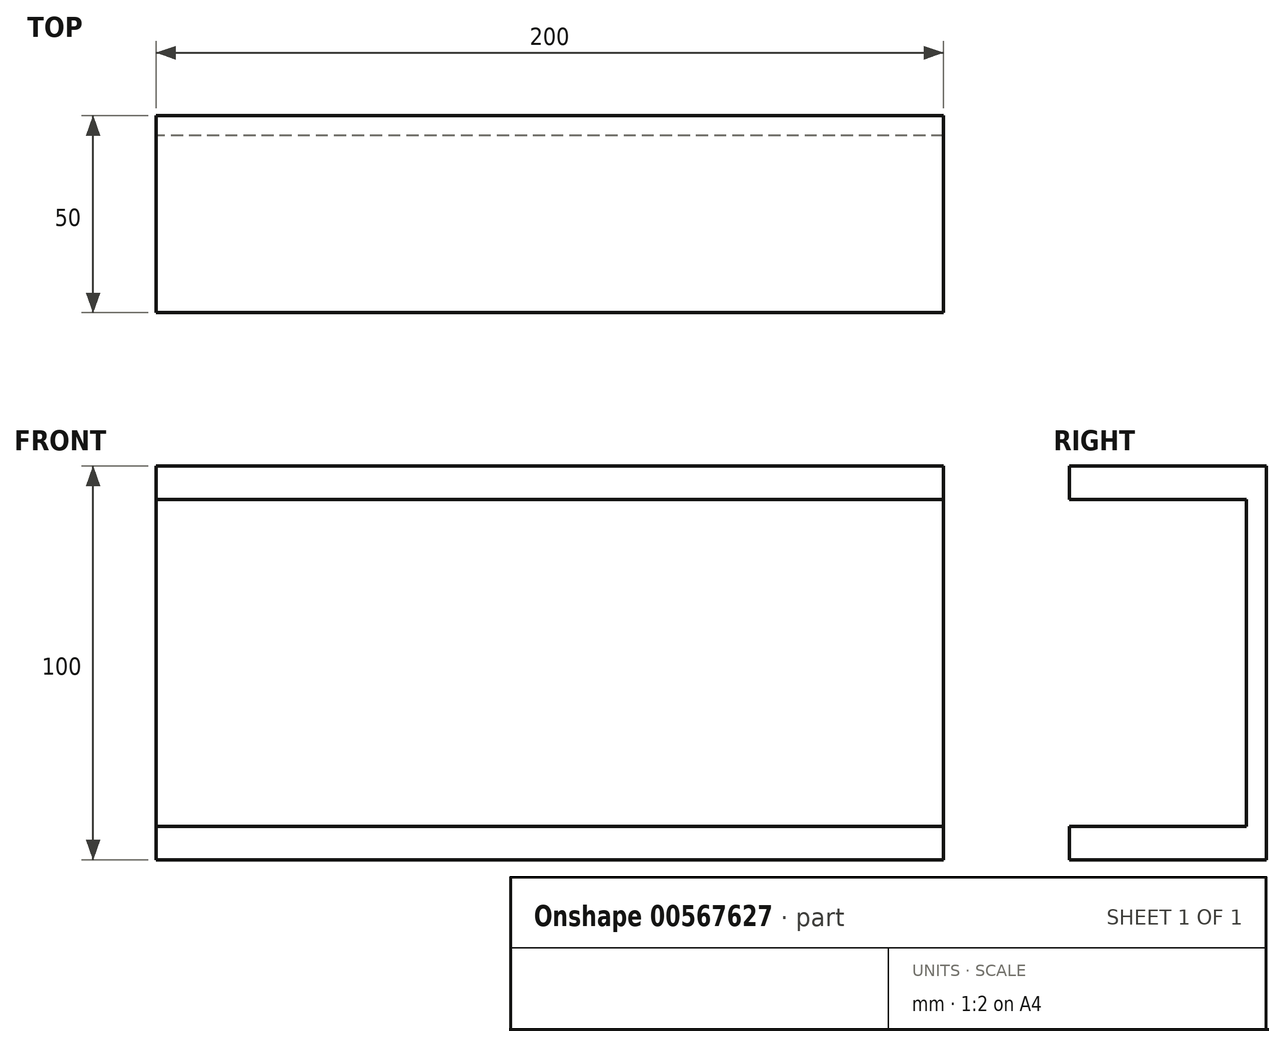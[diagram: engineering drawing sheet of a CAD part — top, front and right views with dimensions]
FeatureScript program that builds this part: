
annotation { "Feature Type Name" : "Feature", "Feature Type Description" : "" }
export const myFeature = defineFeature(function(context is Context, id is Id, definition is map)
    precondition{}
    {
        {
            var Q0;
            Q0=qCreatedBy(makeId("Right.planeOp"),FACE);
            var sketch = newSketch(context, id + "F0", { "sketchPlane" : qUnion([Q0])});
            skLineSegment(sketch, "E0", {"start": v(-45, 25.39) * mm, "end": v(5, 25.39) * mm});
            skLineSegment(sketch, "E1", {"start": v(5, 25.39) * mm, "end": v(5, -74.61) * mm});
            skLineSegment(sketch, "E2", {"start": v(5, -74.61) * mm, "end": v(-45, -74.61) * mm});
            skLineSegment(sketch, "E3", {"start": v(-45, -74.61) * mm, "end": v(-45, -66.11) * mm});
            skLineSegment(sketch, "E4", {"start": v(-45, -66.11) * mm, "end": v(0, -66.11) * mm});
            skLineSegment(sketch, "E5", {"start": v(0, -66.11) * mm, "end": v(0, 16.89) * mm});
            skLineSegment(sketch, "E6", {"start": v(0, 16.89) * mm, "end": v(-45, 16.89) * mm});
            skLineSegment(sketch, "E7", {"start": v(-45, 16.89) * mm, "end": v(-45, 25.39) * mm});
            skSolve(sketch);
        }
        {
            var Q0;
            Q0=makeQuery(id+"F0.imprint","IMPRINT",FACE,{"disambiguationData":[TD([[makeQuery(id+"F0.imprint","IMPRINT",EDGE,{"derivedFrom":sQuery(id+"F0.wireOp",EDGE,"E0")}),-1.0]])]});
            extrude(context, id + "F1", {"entities" : qUnion([Q0]), "depth" : 200 * mm, "offsetDistance" : 25 * mm});
        }
    });
